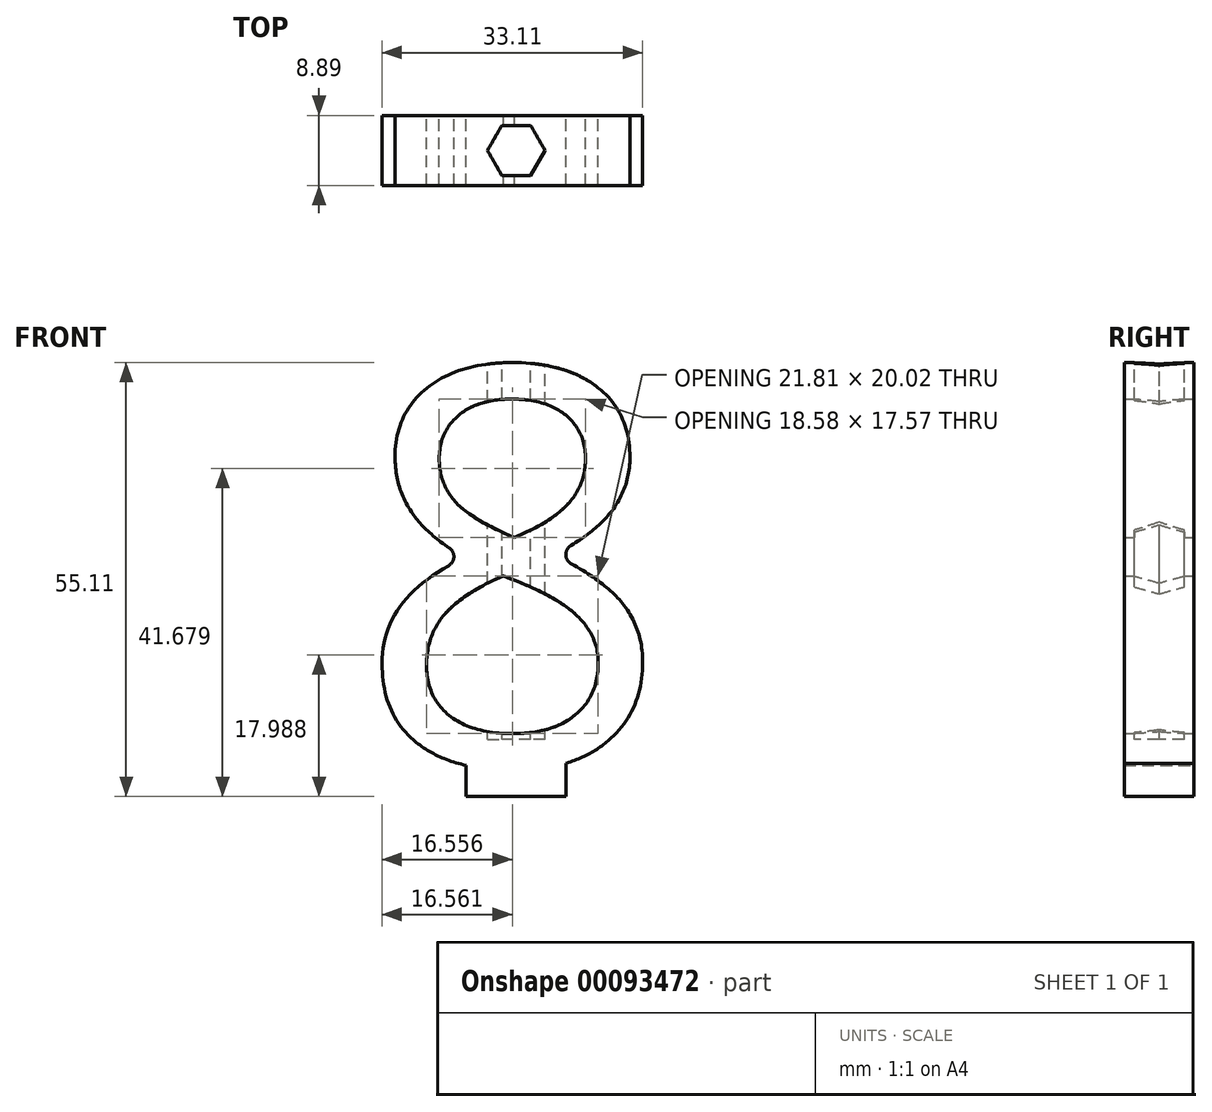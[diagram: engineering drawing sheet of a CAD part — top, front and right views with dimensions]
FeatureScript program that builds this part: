
annotation { "Feature Type Name" : "Feature", "Feature Type Description" : "" }
export const myFeature = defineFeature(function(context is Context, id is Id, definition is map)
    precondition{}
    {
        {
            var Q0;
            Q0=qCreatedBy(makeId("Front.planeOp"),FACE);
            var sketch = newSketch(context, id + "F0", { "sketchPlane" : qUnion([Q0])});
            skText(sketch, "E0", { "text": "8\n", "fontName": "OpenSans-Regular.ttf"});
            const initialGuessF0  = {"E0": [0, 0, 1, 0, 0.0508]};
            skSetInitialGuess(sketch, initialGuessF0);
            skSolve(sketch);
        }
        {
            var Q0;
            Q0=makeQuery(id+"F0.imprint","IMPRINT",FACE,{"disambiguationData":[TD([[makeQuery(id+"F0.imprint","IMPRINT",EDGE,{"derivedFrom":sQuery(id+"F0.wireOp",EDGE,"E0.sketch_text.stroke-0")}),-1.0]])]});
            extrude(context, id + "F1", {"entities" : qUnion([Q0]), "depth" : 8.9 * mm});
        }
        {
            var Q0;
            Q0=qCreatedBy(makeId("Top.planeOp"),FACE);
            var Q1;
            Q1=makeQuery(id+"F1.opExtrude","CAP_VERTEX",VERTEX,{"disambiguationData":[OSD([sQuery(id+"F0.wireOp",EDGE,"E0.sketch_text.stroke-0"),sQuery(id+"F0.wireOp",EDGE,"E0.sketch_text.stroke-14")])],"isStart":false});
            cPlane(context, id + "F2", {"entities" : qUnion([Q0, Q1]), "cplaneType" : CPlaneType.PLANE_POINT, "offset" : 25.4 * mm, "width" : 152.4 * mm, "height" : 152.4 * mm});
        }
        {
            var Q0;
            Q0=qCreatedBy(id+"F2.planeOp",FACE);
            var sketch = newSketch(context, id + "F3", { "sketchPlane" : qUnion([Q0])});
            skLineSegment(sketch, "E1", {"start": v(0, 0) * mm, "end": v(20.63, 0) * mm});
            skLineSegment(sketch, "E2", {"start": v(20.63, 0) * mm, "end": v(20.63, -8.89) * mm});
            skCircle(sketch, "E3.cCircle", {"center": v(20.63, -4.44) * mm, "radius": 3.18 * mm, "construction": true});
            skLineSegment(sketch, "E3.0", {"start": v(18.8, -1.27) * mm, "end": v(22.47, -1.27) * mm});
            skLineSegment(sketch, "E3.1", {"start": v(22.47, -1.27) * mm, "end": v(24.3, -4.44) * mm});
            skLineSegment(sketch, "E3.2", {"start": v(24.3, -4.44) * mm, "end": v(22.47, -7.62) * mm});
            skLineSegment(sketch, "E3.3", {"start": v(22.47, -7.62) * mm, "end": v(18.8, -7.62) * mm});
            skLineSegment(sketch, "E3.4", {"start": v(18.8, -7.62) * mm, "end": v(16.97, -4.44) * mm});
            skLineSegment(sketch, "E3.5", {"start": v(16.97, -4.44) * mm, "end": v(18.8, -1.27) * mm});
            skPoint(sketch, "E3.0.midPoint", {"position": v(20.63, -1.27) * mm});
            skSolve(sketch);
        }
        {
            var Q0;
            {var subQ0=sQuery(id+"F3.wireOp",EDGE,"E3.4");Q0=makeQuery(id+"F3.imprint","IMPRINT",FACE,{"disambiguationData":[TD([[makeQuery(id+"F3.imprint","IMPRINT",EDGE,{"derivedFrom":subQ0}),-1.0]])]});}
            var Q1;
            {var subQ1=sQuery(id+"F3.wireOp",EDGE,"E3.1");Q1=makeQuery(id+"F3.imprint","IMPRINT",FACE,{"disambiguationData":[TD([[makeQuery(id+"F3.imprint","IMPRINT",EDGE,{"derivedFrom":subQ1}),-1.0]])]});}
            extrude(context, id + "F4", {"entities" : qUnion([Q0, Q1]), "operationType" : NewBodyOperationType.REMOVE, "oppositeDirection" : true, "depth" : 47.85 * mm});
        }
        {
            var Q0;
            Q0=makeQuery(id+"F1.opExtrude","SWEPT_EDGE",EDGE,{"disambiguationData":[OSD([sQuery(id+"F0.wireOp",EDGE,"E0.sketch_text.stroke-10"),sQuery(id+"F0.wireOp",EDGE,"E0.sketch_text.stroke-11")])]});
            var Q1;
            Q1=makeQuery(id+"F1.opExtrude","SWEPT_EDGE",EDGE,{"disambiguationData":[OSD([sQuery(id+"F0.wireOp",EDGE,"E0.sketch_text.stroke-3"),sQuery(id+"F0.wireOp",EDGE,"E0.sketch_text.stroke-4")])]});
            fillet(context, id + "F5", {"entities" : qUnion([Q0, Q1]), "radius" : 1.35 * mm, "tangentPropagation" : true, "allowEdgeOverflow" : false});
        }
        {
            var Q0;
            Q0=qCreatedBy(id+"F2.planeOp",FACE);
            var Q1;
            Q1=makeQuery(id+"F1.opExtrude","CAP_VERTEX",VERTEX,{"disambiguationData":[OSD([sQuery(id+"F0.wireOp",EDGE,"E0.sketch_text.stroke-7"),sQuery(id+"F0.wireOp",EDGE,"E0.sketch_text.stroke-8")])],"isStart":false});
            cPlane(context, id + "F6", {"entities" : qUnion([Q0, Q1]), "cplaneType" : CPlaneType.PLANE_POINT, "offset" : 25.4 * mm, "width" : 152.4 * mm, "height" : 152.4 * mm});
        }
        {
            var Q0;
            Q0=qCreatedBy(id+"F6.planeOp",FACE);
            var sketch = newSketch(context, id + "F7", { "sketchPlane" : qUnion([Q0])});
            skLineSegment(sketch, "E4", {"start": v(0, 0) * mm, "end": v(20.62, 0) * mm});
            skLineSegment(sketch, "E5", {"start": v(20.62, 0) * mm, "end": v(20.62, -8.9) * mm});
            skLineSegment(sketch, "E6.bottom", {"start": v(26.97, -8.89) * mm, "end": v(14.27, -8.89) * mm});
            skLineSegment(sketch, "E6.top", {"start": v(26.97, 0) * mm, "end": v(14.27, 0) * mm});
            skLineSegment(sketch, "E6.left", {"start": v(26.97, -8.9) * mm, "end": v(26.97, 0) * mm});
            skLineSegment(sketch, "E6.right", {"start": v(14.27, -8.9) * mm, "end": v(14.27, 0) * mm});
            skPoint(sketch, "E6.middle", {"position": v(20.62, -4.45) * mm});
            skSolve(sketch);
        }
        {
            var Q0;
            {var subQ0=sQuery(id+"F7.wireOp",EDGE,"E5");Q0=makeQuery(id+"F7.imprint","IMPRINT",FACE,{"disambiguationData":[TD([[makeQuery(id+"F7.imprint","IMPRINT",EDGE,{"derivedFrom":subQ0}),-1.0]])]});}
            var Q1;
            {var subQ0=sQuery(id+"F7.wireOp",EDGE,"E5");Q1=makeQuery(id+"F7.imprint","IMPRINT",FACE,{"disambiguationData":[TD([[makeQuery(id+"F7.imprint","IMPRINT",EDGE,{"derivedFrom":subQ0}),1.0]])]});}
            extrude(context, id + "F8", {"entities" : qUnion([Q0, Q1]), "operationType" : NewBodyOperationType.ADD, "depth" : 2.72 * mm, "hasSecondDirection" : true, "secondDirectionOppositeDirection" : true, "secondDirectionDepth" : 3.33 * mm});
        }
    });
